# Revit family: Faucet_Single_Control-American_Standard-Grayson-7612350_Series
name_source: partatom
category: Plumbing Fixtures
units: mm (PartAtom-declared; Revit-internal decimal feet)

## family parameters
Always vertical = No
Cut with Voids When Loaded = No
OmniClass Number = 23.45.55.14
OmniClass Title = Single Faucets
Part Type = Normal
Room Calculation Point = No
Round Connector Dimension = Use Diameter
Shared = Yes
Work Plane-Based = Yes

## types (2) — shared parameters
1660152.075 Deckplate = Yes
ADA Compliant = Yes
Assembly Code = D2020300
CEC Compliant = Yes
CW Connection = No
CWFU = 1.5
CalGreen Compliant = Yes
Compliance Certifications = These products meet or exceed ANSI A117.1, ASME A112.18.1,CSA B125.1,NSF 61/Section 9,NSF 372
Deck Plate Height = 3/8"
Deck Plate Material = Metal-American_Standard-075-Stainless_Steel
Default Elevation = 0"
Description = Grayson™ Semi-Professional Single-Handle Kitchen Faucet
Flow Rate = 1.8 gpm (6.8 Lpm)
HW Connection = No
HWFU = 1.5
Height = 20 5/8"
Installation Type = Deck Mounted
Length = 8 1/2"
M950328-0750A Soap Dispenser = Yes
Manufacturer = American Standard
Product Documentation Link = https://americanstandard.box.com
Product Page URL = https://www.americanstandard-us.com
Soap Dispenser Width = 10"
Tempered Water Connection = Yes
Tempered Water Connection Diameter = 3/8"
URL = http://www.americanstandard.com
Vent Connection = No
Waste Connection = No
Width = 10 9/16"
zero-valued in all types: WFU

## per-type parameters (varying)
| type | Finish | Material |
| 7612350.075 | Metal-American_Standard-075-Stainless_Steel | Metal-American_Standard-075-Stainless_Steel |
| 7612350.243 | Metal-American Standard-243-Matte Black | Metal-American Standard-243-Matte Black |

note: column(s) folded — value = type name in every type: Model

## geometry (parser evidence)
native form markers: Sweep x5
no freeform markers — native parametric forms only
